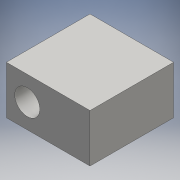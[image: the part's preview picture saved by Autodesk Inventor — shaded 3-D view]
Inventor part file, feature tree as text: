
AUTODESK INVENTOR PART (.ipt)
format: ipt  version: 2016 SP1 (Build 200210100, 210)  size: 90,624 bytes
history: native  units: mm
features: extrude x1, hole x1, sketch x1
ambient origin geometry x8: Origin, YZ Plane, XZ Plane, XY Plane, X Axis, Y Axis, Z Axis, Center Point
bodies: Solid1 (feature_tree)
feature tree (3):
  extrude  "Extrusion1"  Depth=20.0mm
  hole  "Hole1"  [1 undecoded]
  sketch  "Sketch1"  dims[d0=20.0mm d1=20.0mm d2=10.0mm d3=10.0mm d4=11.5mm d5=0.0mm d6=5.0mm d7=5.75mm d8=6.0mm d9=6.0mm d10=4.0mm d11=2.0mm d12=90.0deg d13=8.0mm d14=20.594885mm]
note: 1 required parameter value undecoded (feature->parameter linkage not recoverable at this tier; creation-order binding heuristic only, values carry confidence <= 0.55)
